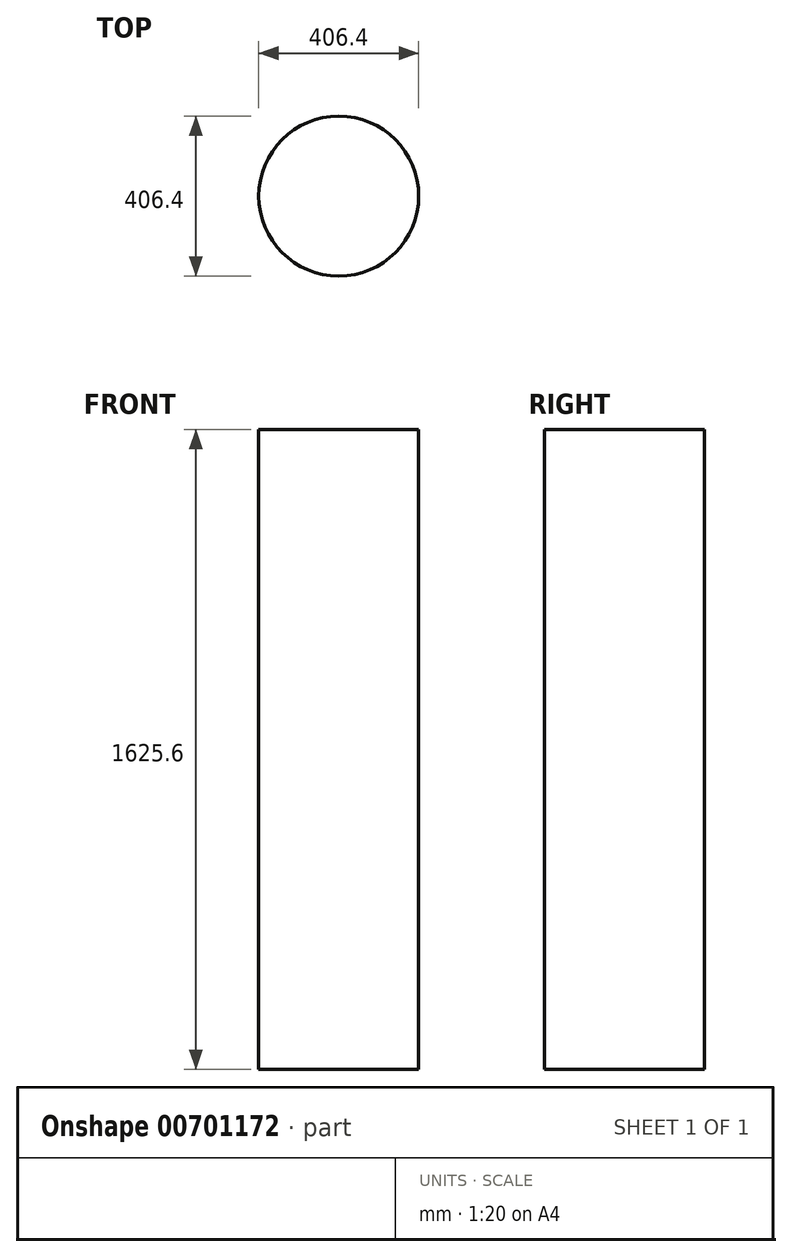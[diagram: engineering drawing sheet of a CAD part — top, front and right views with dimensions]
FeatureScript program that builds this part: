
annotation { "Feature Type Name" : "Feature", "Feature Type Description" : "" }
export const myFeature = defineFeature(function(context is Context, id is Id, definition is map)
    precondition{}
    {
        {
            var Q0;
            Q0=qCreatedBy(makeId("Top.planeOp"),FACE);
            var sketch = newSketch(context, id + "F0", { "sketchPlane" : qUnion([Q0])});
            skCircle(sketch, "E0", {"center": v(0, 0) * mm, "radius": 203.2 * mm});
            skSolve(sketch);
        }
        {
            var Q0;
            Q0 = qSketchRegion(id + "F0", true);
            extrude(context, id + "F1", {"entities" : qUnion([Q0]), "depth" : 1625.6 * mm, "offsetDistance" : 25.4 * mm});
        }
    });
